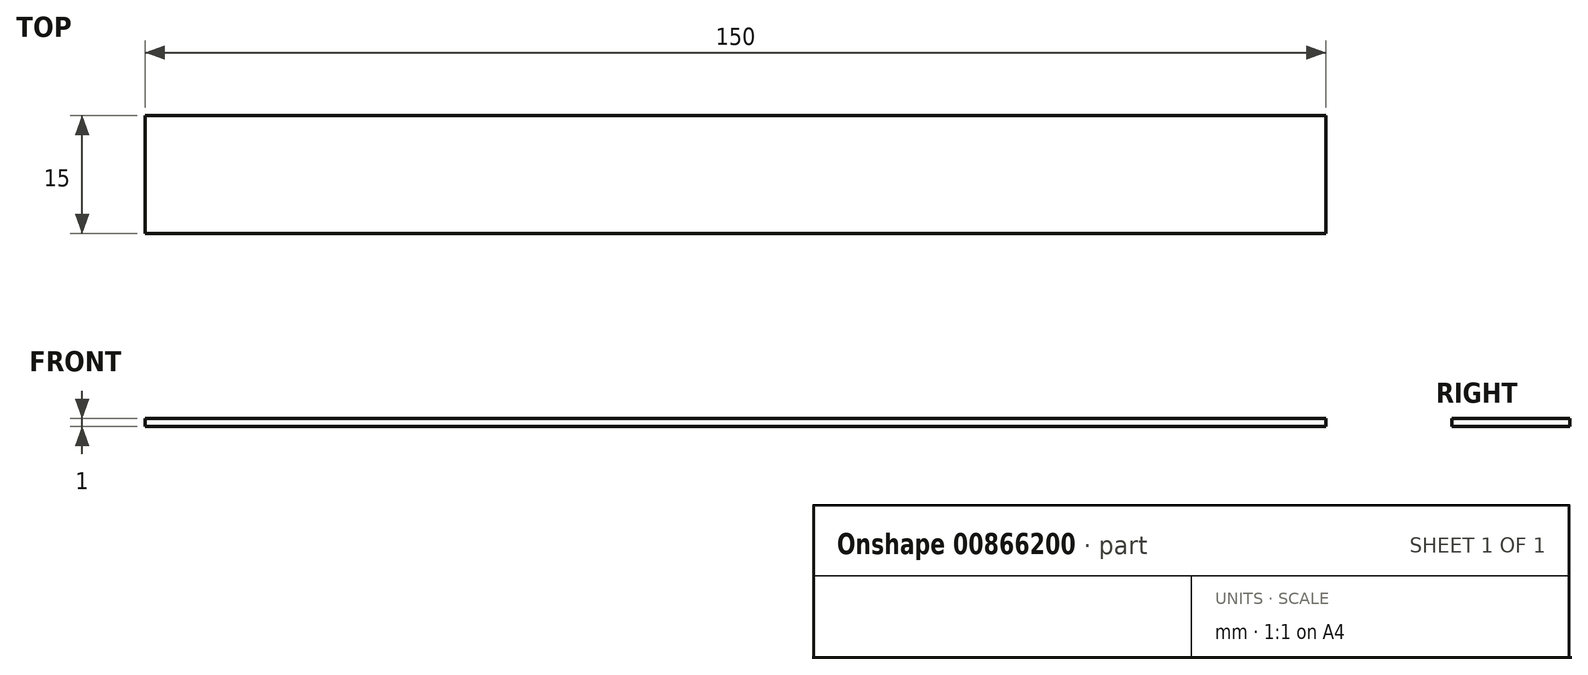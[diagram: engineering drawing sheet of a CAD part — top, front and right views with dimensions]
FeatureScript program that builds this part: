
annotation { "Feature Type Name" : "Feature", "Feature Type Description" : "" }
export const myFeature = defineFeature(function(context is Context, id is Id, definition is map)
    precondition{}
    {
        {
            var Q0;
            Q0=qCreatedBy(makeId("Top.planeOp"),FACE);
            var sketch = newSketch(context, id + "F0", { "sketchPlane" : qUnion([Q0])});
            skLineSegment(sketch, "E0.bottom", {"start": v(-75, 7.5) * mm, "end": v(75, 7.5) * mm});
            skLineSegment(sketch, "E0.top", {"start": v(-75, -7.5) * mm, "end": v(75, -7.5) * mm});
            skLineSegment(sketch, "E0.left", {"start": v(-75, 7.5) * mm, "end": v(-75, -7.5) * mm});
            skLineSegment(sketch, "E0.right", {"start": v(75, 7.5) * mm, "end": v(75, -7.5) * mm});
            skSolve(sketch);
        }
        {
            var Q0;
            Q0=makeQuery(id+"F0.imprint","IMPRINT",FACE,{"disambiguationData":[TD([[makeQuery(id+"F0.imprint","IMPRINT",EDGE,{"derivedFrom":sQuery(id+"F0.wireOp",EDGE,"E0.bottom")}),-1.0]])]});
            extrude(context, id + "F1", {"entities" : qUnion([Q0]), "depth" : 1 * mm, "offsetDistance" : 25 * mm});
        }
    });
